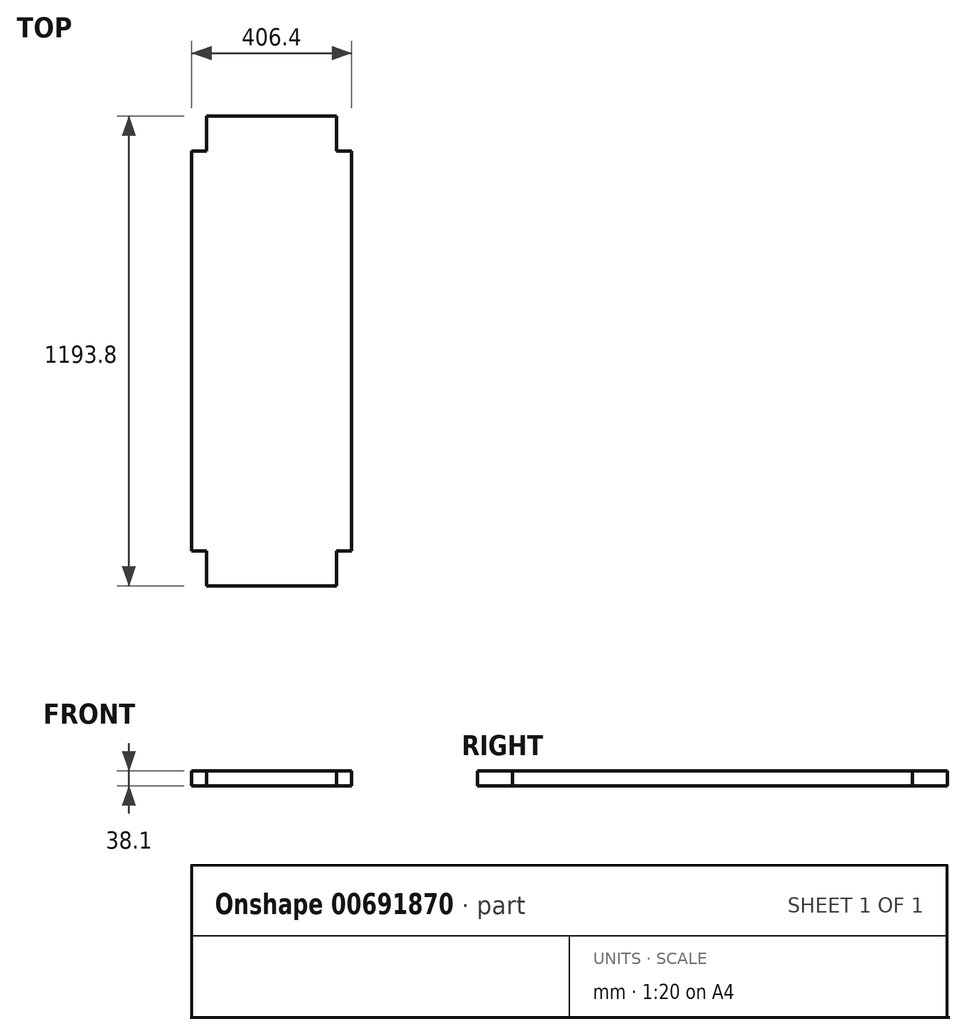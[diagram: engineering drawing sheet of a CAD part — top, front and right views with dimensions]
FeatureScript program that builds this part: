
annotation { "Feature Type Name" : "Feature", "Feature Type Description" : "" }
export const myFeature = defineFeature(function(context is Context, id is Id, definition is map)
    precondition{}
    {
        {
            var Q0;
            Q0=qCreatedBy(makeId("Top.planeOp"),FACE);
            var sketch = newSketch(context, id + "F0", { "sketchPlane" : qUnion([Q0])});
            skLineSegment(sketch, "E0.bottom", {"start": v(0, 0) * mm, "end": v(406.4, 0) * mm, "construction": true});
            skLineSegment(sketch, "E0.top", {"start": v(0, 1295.4) * mm, "end": v(406.4, 1295.4) * mm, "construction": true});
            skLineSegment(sketch, "E0.left", {"start": v(0, 0) * mm, "end": v(0, 1295.4) * mm, "construction": true});
            skLineSegment(sketch, "E0.right", {"start": v(406.4, 0) * mm, "end": v(406.4, 1295.4) * mm, "construction": true});
            skLineSegment(sketch, "E1", {"start": v(0, 628.65) * mm, "end": v(406.4, 628.65) * mm, "construction": true});
            skLineSegment(sketch, "E2", {"start": v(406.4, 717.55) * mm, "end": v(0, 717.55) * mm, "construction": true});
            skLineSegment(sketch, "E3", {"start": v(0, 50.8) * mm, "end": v(38.1, 50.8) * mm, "construction": true});
            skLineSegment(sketch, "E4", {"start": v(0, 1244.6) * mm, "end": v(406.4, 1244.6) * mm, "construction": true});
            skLineSegment(sketch, "E5", {"start": v(0, 1155.7) * mm, "end": v(406.4, 1155.7) * mm, "construction": true});
            skLineSegment(sketch, "E6", {"start": v(0, 139.7) * mm, "end": v(406.4, 139.7) * mm, "construction": true});
            skLineSegment(sketch, "E7", {"start": v(368.3, 1244.6) * mm, "end": v(368.3, 50.8) * mm, "construction": true});
            skLineSegment(sketch, "E8", {"start": v(0, 1200.15) * mm, "end": v(38.1, 1200.15) * mm, "construction": true});
            skLineSegment(sketch, "E9", {"start": v(0, 95.25) * mm, "end": v(368.3, 95.25) * mm, "construction": true});
            skLineSegment(sketch, "E10", {"start": v(38.1, 1295.4) * mm, "end": v(38.1, 0) * mm, "construction": true});
            skLineSegment(sketch, "E11", {"start": v(0, 717.55) * mm, "end": v(0, 1155.7) * mm});
            skLineSegment(sketch, "E12", {"start": v(38.1, 1155.7) * mm, "end": v(38.1, 1200.15) * mm});
            skLineSegment(sketch, "E13", {"start": v(38.1, 1200.15) * mm, "end": v(368.3, 1200.15) * mm});
            skLineSegment(sketch, "E14", {"start": v(368.3, 1155.7) * mm, "end": v(406.4, 1155.7) * mm});
            skLineSegment(sketch, "E15", {"start": v(406.4, 717.55) * mm, "end": v(368.3, 717.55) * mm});
            skLineSegment(sketch, "E16", {"start": v(368.3, 717.55) * mm, "end": v(368.3, 628.65) * mm});
            skLineSegment(sketch, "E17", {"start": v(368.3, 628.65) * mm, "end": v(406.4, 628.65) * mm});
            skLineSegment(sketch, "E18", {"start": v(0, 1155.7) * mm, "end": v(38.1, 1155.7) * mm});
            skLineSegment(sketch, "E19", {"start": v(368.3, 1200.15) * mm, "end": v(368.3, 1155.7) * mm});
            skLineSegment(sketch, "E20", {"start": v(406.4, 1155.7) * mm, "end": v(406.4, 717.55) * mm});
            skLineSegment(sketch, "E21", {"start": v(406.4, 628.65) * mm, "end": v(406.4, 139.7) * mm});
            skLineSegment(sketch, "E22", {"start": v(406.4, 139.7) * mm, "end": v(368.3, 139.7) * mm});
            skLineSegment(sketch, "E23", {"start": v(368.3, 139.7) * mm, "end": v(368.3, 95.25) * mm});
            skLineSegment(sketch, "E24", {"start": v(368.3, 95.25) * mm, "end": v(38.1, 95.25) * mm});
            skLineSegment(sketch, "E25", {"start": v(38.1, 95.25) * mm, "end": v(38.1, 139.7) * mm});
            skLineSegment(sketch, "E26", {"start": v(38.1, 139.7) * mm, "end": v(0, 139.7) * mm});
            skLineSegment(sketch, "E27", {"start": v(0, 628.65) * mm, "end": v(0, 139.7) * mm});
            skLineSegment(sketch, "E28", {"start": v(0, 628.65) * mm, "end": v(38.1, 628.65) * mm});
            skLineSegment(sketch, "E29", {"start": v(38.1, 628.65) * mm, "end": v(38.1, 717.55) * mm});
            skLineSegment(sketch, "E30", {"start": v(38.1, 717.55) * mm, "end": v(0, 717.55) * mm});
            skLineSegment(sketch, "E31.trimOffspring", {"start": v(368.3, 50.8) * mm, "end": v(406.4, 50.8) * mm, "construction": true});
            skLineSegment(sketch, "E32", {"start": v(38.1, 95.25) * mm, "end": v(38.1, 50.8) * mm});
            skLineSegment(sketch, "E33", {"start": v(38.1, 50.8) * mm, "end": v(368.3, 50.8) * mm});
            skLineSegment(sketch, "E34", {"start": v(368.3, 50.8) * mm, "end": v(368.3, 95.25) * mm});
            skLineSegment(sketch, "E35", {"start": v(38.1, 1200.15) * mm, "end": v(38.1, 1244.6) * mm});
            skLineSegment(sketch, "E36", {"start": v(38.1, 1244.6) * mm, "end": v(368.3, 1244.6) * mm});
            skLineSegment(sketch, "E37", {"start": v(368.3, 1244.6) * mm, "end": v(368.3, 1200.15) * mm});
            skLineSegment(sketch, "E38", {"start": v(406.4, 717.55) * mm, "end": v(406.4, 628.65) * mm});
            skLineSegment(sketch, "E39", {"start": v(0, 717.55) * mm, "end": v(0, 628.65) * mm});
            skSolve(sketch);
        }
        {
            var Q0;
            Q0 = qSketchRegion(id + "F0", true);
            extrude(context, id + "F1", {"entities" : qUnion([Q0]), "depth" : 38.1 * mm, "offsetDistance" : 25.4 * mm});
        }
    });
